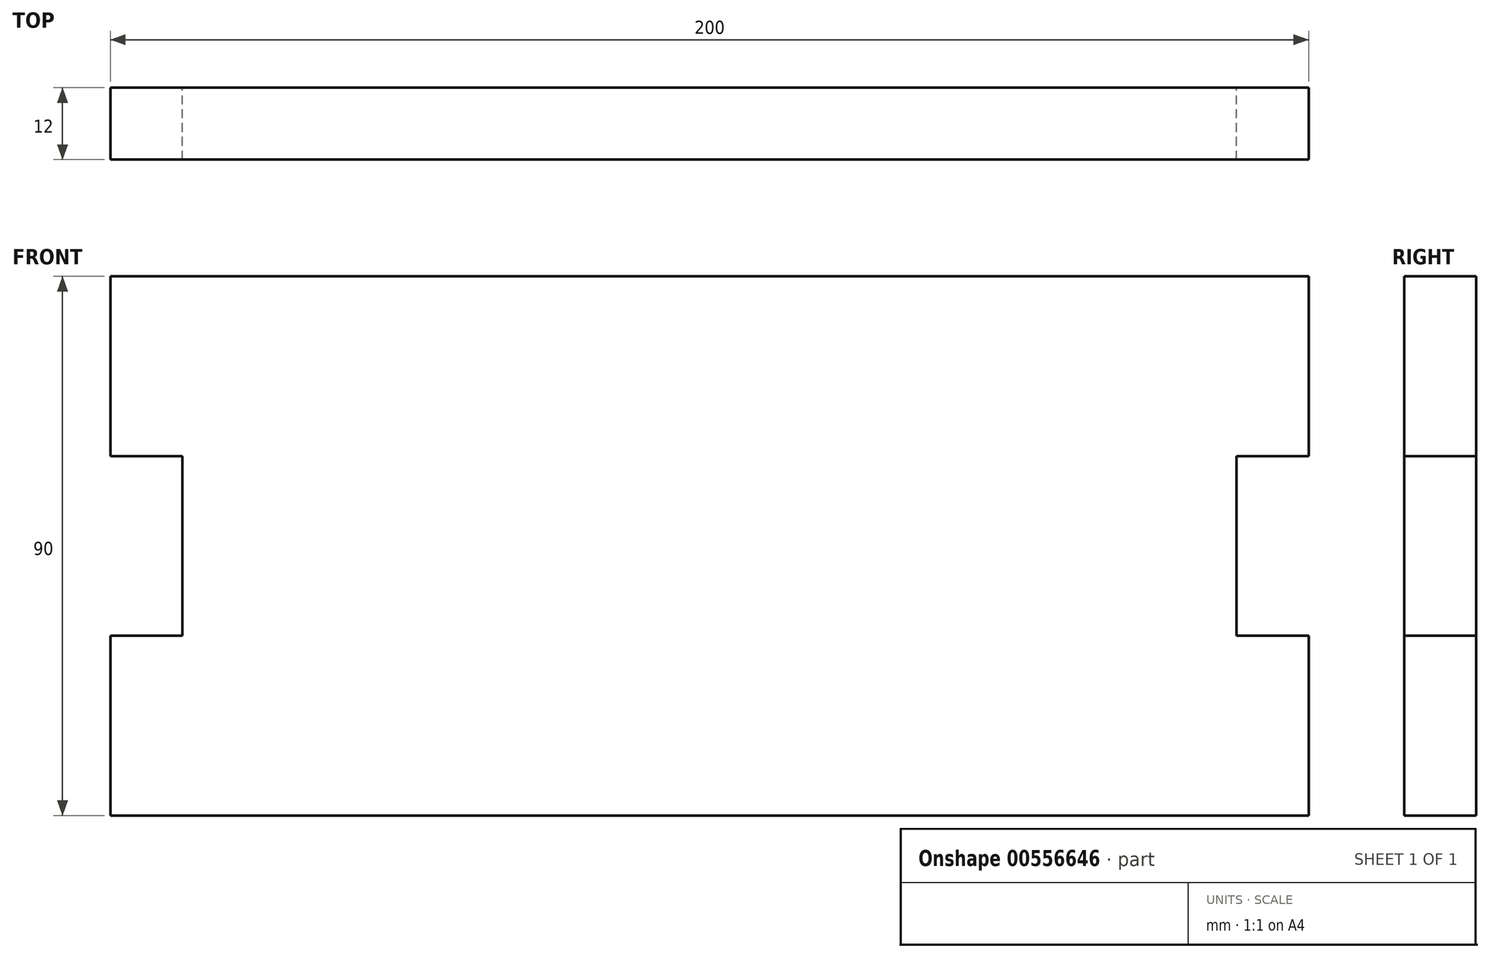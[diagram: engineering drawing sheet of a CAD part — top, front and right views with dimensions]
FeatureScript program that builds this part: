
annotation { "Feature Type Name" : "Feature", "Feature Type Description" : "" }
export const myFeature = defineFeature(function(context is Context, id is Id, definition is map)
    precondition{}
    {
        {
            var Q0;
            Q0=qCreatedBy(makeId("Front.planeOp"),FACE);
            var sketch = newSketch(context, id + "F0", { "sketchPlane" : qUnion([Q0])});
            skLineSegment(sketch, "E0", {"start": v(0, 0) * mm, "end": v(0, 30) * mm});
            skLineSegment(sketch, "E1", {"start": v(0, 30) * mm, "end": v(12, 30) * mm});
            skLineSegment(sketch, "E2", {"start": v(12, 30) * mm, "end": v(12, 60) * mm});
            skLineSegment(sketch, "E3", {"start": v(12, 60) * mm, "end": v(0, 60) * mm});
            skLineSegment(sketch, "E4", {"start": v(0, 60) * mm, "end": v(0, 90) * mm});
            skLineSegment(sketch, "E5", {"start": v(0, 90) * mm, "end": v(12, 90) * mm});
            skLineSegment(sketch, "E6", {"start": v(0, 0) * mm, "end": v(100, 0) * mm});
            skLineSegment(sketch, "E7", {"start": v(12, 90) * mm, "end": v(100, 90) * mm});
            skLineSegment(sketch, "E8", {"start": v(100, 90) * mm, "end": v(100, 0) * mm});
            skLineSegment(sketch, "E9.MirrorCS", {"start": v(188, 30) * mm, "end": v(188, 60) * mm});
            skLineSegment(sketch, "E10.MirrorCS", {"start": v(188, 60) * mm, "end": v(200, 60) * mm});
            skLineSegment(sketch, "E11.MirrorCS", {"start": v(200, 0) * mm, "end": v(200, 30) * mm});
            skLineSegment(sketch, "E12.MirrorCS", {"start": v(200, 60) * mm, "end": v(200, 90) * mm});
            skLineSegment(sketch, "E13.MirrorCS", {"start": v(200, 90) * mm, "end": v(188, 90) * mm});
            skLineSegment(sketch, "E14.MirrorCS", {"start": v(200, 30) * mm, "end": v(188, 30) * mm});
            skLineSegment(sketch, "E15.MirrorCS", {"start": v(188, 90) * mm, "end": v(100, 90) * mm});
            skLineSegment(sketch, "E16.MirrorCS", {"start": v(200, 0) * mm, "end": v(100, 0) * mm});
            skSolve(sketch);
        }
        {
            var Q0;
            Q0=makeQuery(id+"F0.imprint","IMPRINT",FACE,{"disambiguationData":[TD([[makeQuery(id+"F0.imprint","IMPRINT",EDGE,{"derivedFrom":sQuery(id+"F0.wireOp",EDGE,"E0")}),-1.0]])]});
            var Q1;
            Q1=makeQuery(id+"F0.imprint","IMPRINT",FACE,{"disambiguationData":[TD([[makeQuery(id+"F0.imprint","IMPRINT",EDGE,{"derivedFrom":sQuery(id+"F0.wireOp",EDGE,"E8")}),1.0]])]});
            extrude(context, id + "F1", {"entities" : qUnion([Q0, Q1]), "endBound" : BoundingType.SYMMETRIC, "depth" : 12 * mm, "offsetDistance" : 25 * mm});
        }
    });
